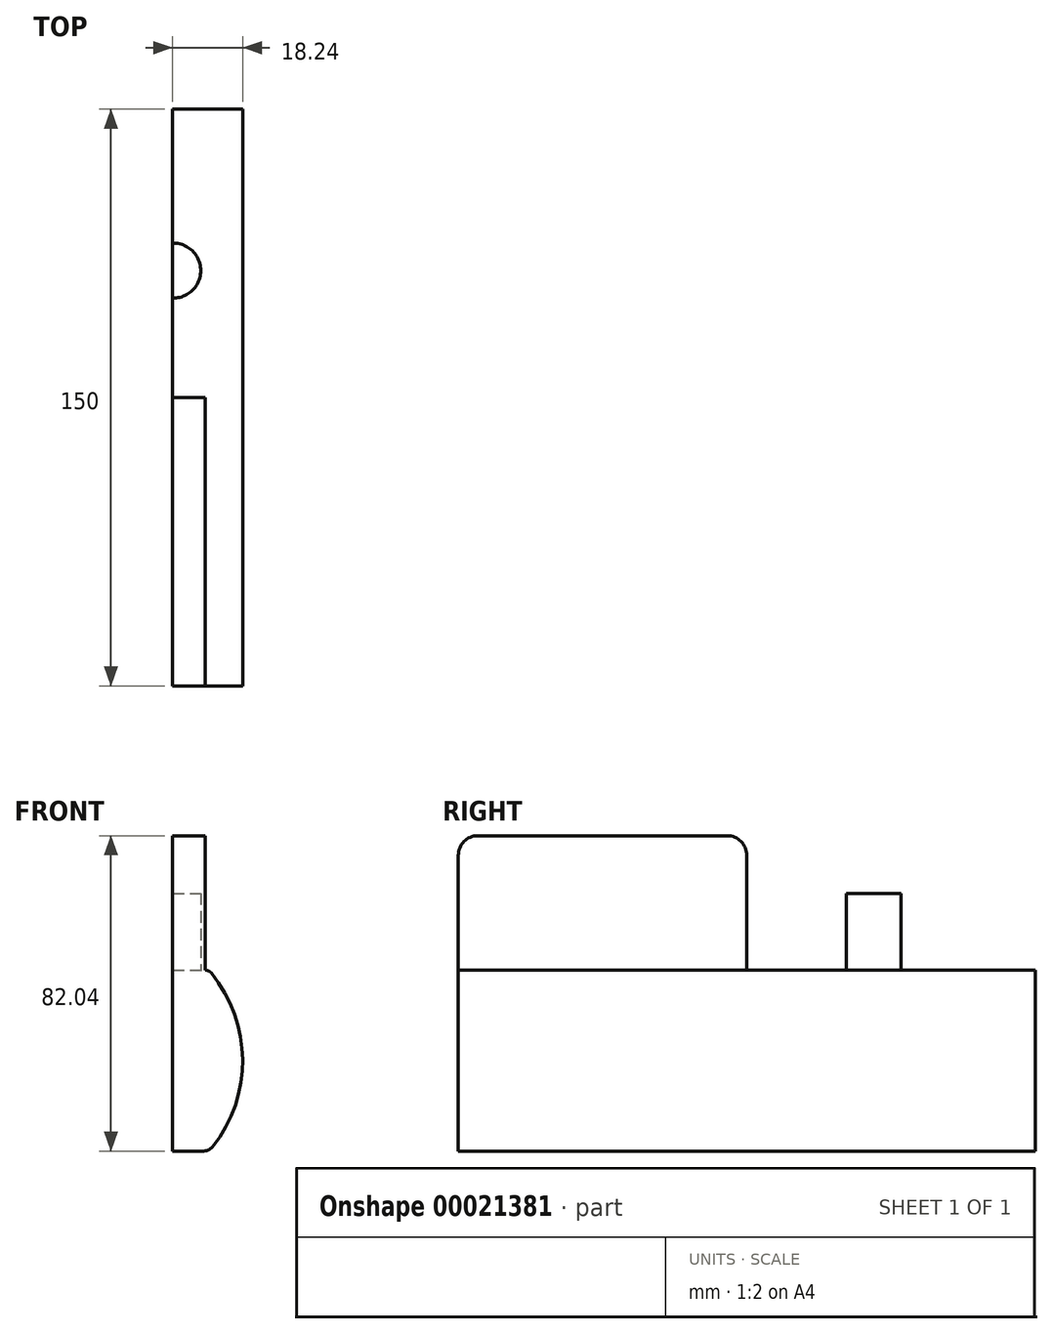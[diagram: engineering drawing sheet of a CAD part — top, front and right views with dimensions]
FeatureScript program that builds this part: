
annotation { "Feature Type Name" : "Feature", "Feature Type Description" : "" }
export const myFeature = defineFeature(function(context is Context, id is Id, definition is map)
    precondition{}
    {
        {
            var Q0;
            Q0=qCreatedBy(makeId("Front.planeOp"),FACE);
            var sketch = newSketch(context, id + "F0", { "sketchPlane" : qUnion([Q0])});
            skLineSegment(sketch, "E0.bottom", {"start": v(0, 0) * mm, "end": v(9.5, 0) * mm});
            skLineSegment(sketch, "E0.top", {"start": v(0, 47.04) * mm, "end": v(9.5, 47.04) * mm});
            skLineSegment(sketch, "E0.left", {"start": v(0, 0) * mm, "end": v(0, 47.04) * mm});
            skArc(sketch, "E1", {"start": v(9.5, 0) * mm, "mid": v(18.24, 23.52) * mm, "end": v(9.5, 47.04) * mm});
            skSolve(sketch);
        }
        {
            var Q0;
            Q0=makeQuery(id+"F0.imprint","IMPRINT",FACE,{"disambiguationData":[TD([[makeQuery(id+"F0.imprint","IMPRINT",EDGE,{"derivedFrom":sQuery(id+"F0.wireOp",EDGE,"E0.bottom")}),1.0]])]});
            extrude(context, id + "F1", {"entities" : qUnion([Q0]), "depth" : 150 * mm});
        }
        {
            var Q0;
            Q0=makeQuery(id+"F1.opExtrude","SWEPT_FACE",FACE,{"disambiguationData":[OSD([sQuery(id+"F0.wireOp",EDGE,"E0.top")])]});
            var sketch = newSketch(context, id + "F2", { "sketchPlane" : qUnion([Q0])});
            skArc(sketch, "E2", {"start": v(0, -49.14) * mm, "mid": v(7.34, -41.97) * mm, "end": v(0, -34.8) * mm});
            skSolve(sketch);
        }
        {
            var Q0;
            Q0 = qSketchRegion(id + "F2", true);
            var Q1;
            {var subQ1=sQuery(id+"F2.wireOp",EDGE,"E2");Q1=makeQuery(id+"F2.imprint","IMPRINT",FACE,{"disambiguationData":[TD([[makeQuery(id+"F2.imprint","IMPRINT",EDGE,{"derivedFrom":subQ1}),1.0]])]});}
            extrude(context, id + "F3", {"entities" : qUnion([Q0, Q1]), "operationType" : NewBodyOperationType.ADD, "depth" : 20 * mm});
        }
        {
            var Q0;
            Q0=makeQuery(id+"F1.opExtrude","SWEPT_EDGE",EDGE,{"disambiguationData":[OSD([sQuery(id+"F0.wireOp",EDGE,"E0.top"),sQuery(id+"F0.wireOp",EDGE,"E1")])]});
            fillet(context, id + "F4", {"entities" : qUnion([Q0]), "radius" : 2 * mm, "tangentPropagation" : true, "allowEdgeOverflow" : false});
        }
        {
            var Q0;
            Q0=makeQuery(id+"F1.opExtrude","SWEPT_EDGE",EDGE,{"disambiguationData":[OSD([sQuery(id+"F0.wireOp",EDGE,"E0.bottom"),sQuery(id+"F0.wireOp",EDGE,"E1")])]});
            fillet(context, id + "F5", {"entities" : qUnion([Q0]), "radius" : 3 * mm, "tangentPropagation" : true, "allowEdgeOverflow" : false});
        }
        {
            var Q0;
            Q0=makeQuery(id+"F1.opExtrude","SWEPT_FACE",FACE,{"disambiguationData":[OSD([sQuery(id+"F0.wireOp",EDGE,"E0.top")])]});
            var sketch = newSketch(context, id + "F6", { "sketchPlane" : qUnion([Q0])});
            skLineSegment(sketch, "E3.bottom", {"start": v(0, -150) * mm, "end": v(8.57, -150) * mm});
            skLineSegment(sketch, "E3.top", {"start": v(0, -75) * mm, "end": v(8.57, -75) * mm});
            skLineSegment(sketch, "E3.left", {"start": v(0, -150) * mm, "end": v(0, -75) * mm});
            skLineSegment(sketch, "E3.right", {"start": v(8.57, -150) * mm, "end": v(8.57, -75) * mm});
            skSolve(sketch);
        }
        {
            var Q0;
            Q0=makeQuery(id+"F6.imprint","IMPRINT",FACE,{"disambiguationData":[TD([[makeQuery(id+"F6.imprint","IMPRINT",EDGE,{"derivedFrom":sQuery(id+"F6.wireOp",EDGE,"E3.bottom")}),1.0]])]});
            extrude(context, id + "F7", {"entities" : qUnion([Q0]), "operationType" : NewBodyOperationType.ADD, "depth" : 35 * mm});
        }
        {
            var Q0;
            Q0=makeQuery(id+"F7.opExtrude","CAP_EDGE",EDGE,{"disambiguationData":[OSD([sQuery(id+"F6.wireOp",EDGE,"E3.top")])],"isStart":false});
            fillet(context, id + "F8", {"entities" : qUnion([Q0]), "radius" : 5.08 * mm, "tangentPropagation" : true, "allowEdgeOverflow" : false});
        }
        {
            var Q0;
            Q0=makeQuery(id+"F7.opExtrude","CAP_EDGE",EDGE,{"disambiguationData":[OSD([sQuery(id+"F6.wireOp",EDGE,"E3.bottom")])],"isStart":false});
            fillet(context, id + "F9", {"entities" : qUnion([Q0]), "radius" : 5.08 * mm, "tangentPropagation" : true, "allowEdgeOverflow" : false});
        }
    });
